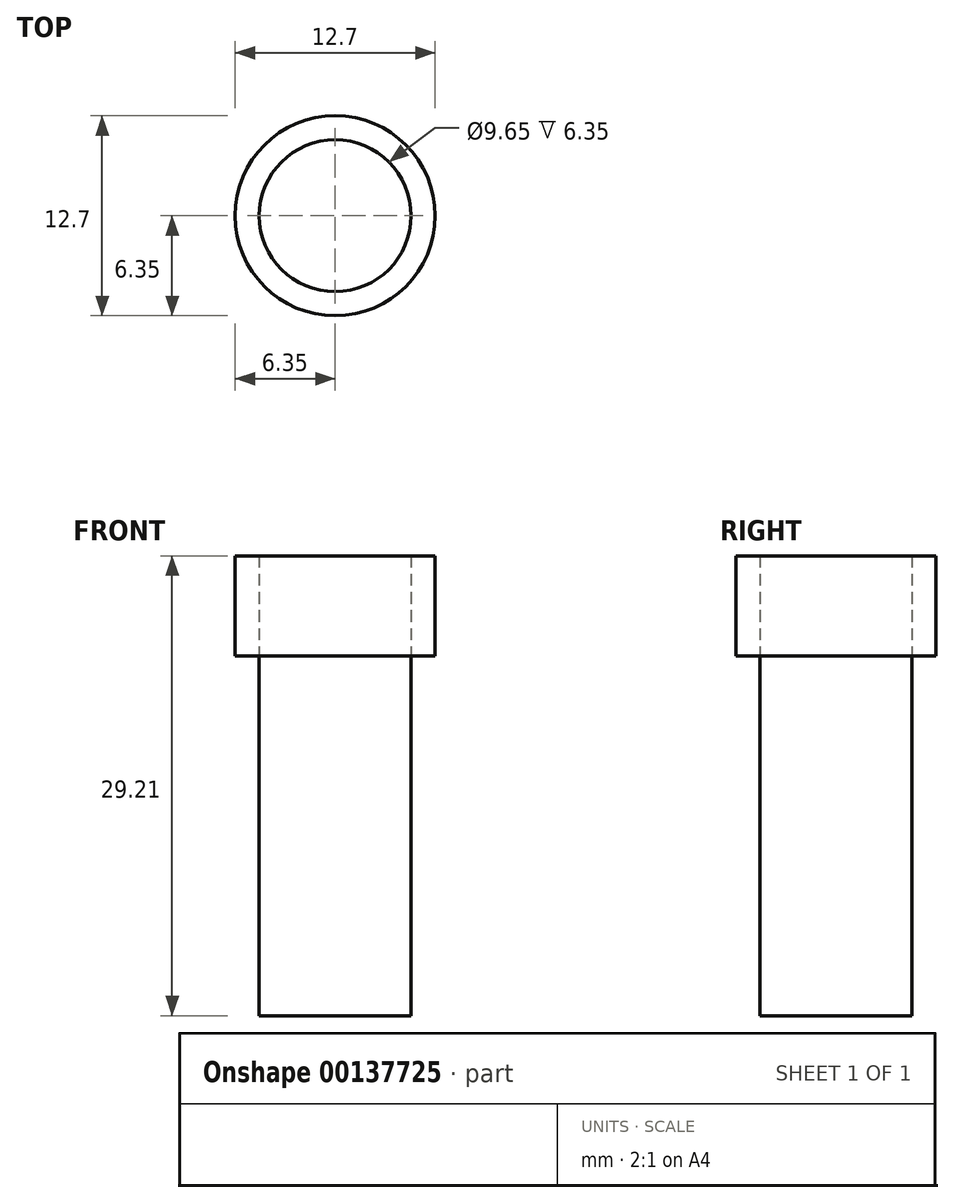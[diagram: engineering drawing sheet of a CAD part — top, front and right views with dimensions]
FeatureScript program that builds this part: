
annotation { "Feature Type Name" : "Feature", "Feature Type Description" : "" }
export const myFeature = defineFeature(function(context is Context, id is Id, definition is map)
    precondition{}
    {
        {
            var Q0;
            Q0=qCreatedBy(makeId("Top.planeOp"),FACE);
            var sketch = newSketch(context, id + "F0", { "sketchPlane" : qUnion([Q0])});
            skCircle(sketch, "E0", {"center": v(0, 0) * mm, "radius": 4.83 * mm});
            skSolve(sketch);
        }
        {
            var Q0;
            Q0=makeQuery(id+"F0.imprint","IMPRINT",FACE,{"disambiguationData":[TD([[makeQuery(id+"F0.imprint","IMPRINT",EDGE,{"derivedFrom":sQuery(id+"F0.wireOp",EDGE,"E0")}),1.0]])]});
            var Q1;
            Q1=qSketchRegion(id+"F2",true);
            extrude(context, id + "F1", {"entities" : qUnion([Q0, Q1]), "depth" : 22.86 * mm});
        }
        {
            var Q0;
            Q0=makeQuery(id+"F1.opExtrude","CAP_FACE",FACE,{"disambiguationData":[OSD([sQuery(id+"F0.wireOp",EDGE,"E0")])],"isStart":false});
            var sketch = newSketch(context, id + "F2", { "sketchPlane" : qUnion([Q0])});
            skCircle(sketch, "E1", {"center": v(0, 0) * mm, "radius": 6.35 * mm});
            skSolve(sketch);
        }
        {
            var Q0;
            Q0=makeQuery(id+"F2.imprint","IMPRINT",FACE,{"disambiguationData":[TD([[makeQuery(id+"F2.imprint","IMPRINT",EDGE,{"derivedFrom":sQuery(id+"F2.wireOp",EDGE,"E1")}),1.0]])]});
            extrude(context, id + "F3", {"entities" : qUnion([Q0]), "depth" : 6.35 * mm});
        }
        {
            var Q0;
            Q0=makeQuery(id+"F1.opExtrude","CAP_FACE",FACE,{"disambiguationData":[OSD([sQuery(id+"F0.wireOp",EDGE,"E0")])],"isStart":false});
            extrude(context, id + "F4", {"entities" : qUnion([Q0]), "depth" : 6.35 * mm});
        }
    });
